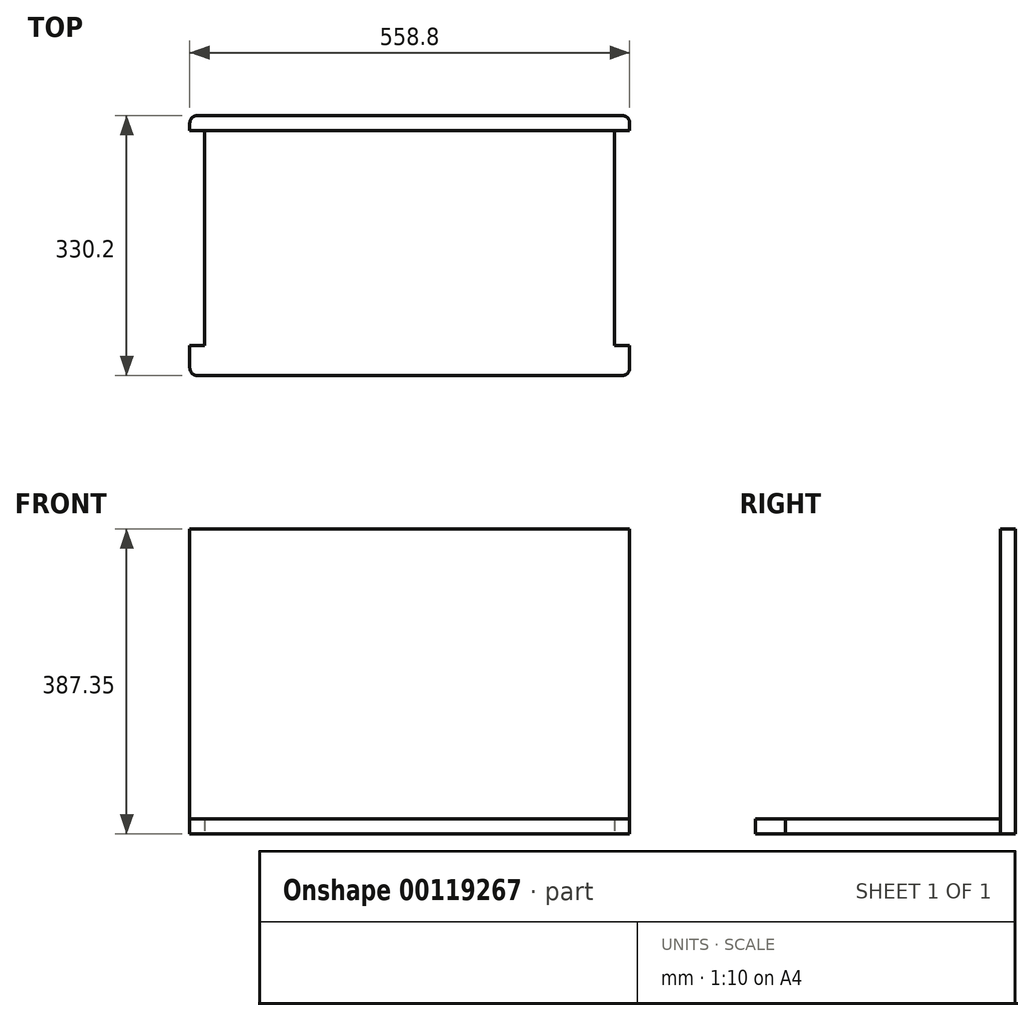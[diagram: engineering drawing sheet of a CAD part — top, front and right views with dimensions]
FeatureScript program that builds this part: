
annotation { "Feature Type Name" : "Feature", "Feature Type Description" : "" }
export const myFeature = defineFeature(function(context is Context, id is Id, definition is map)
    precondition{}
    {
        {
            var Q0;
            Q0=qCreatedBy(makeId("Top.planeOp"),FACE);
            var sketch = newSketch(context, id + "F0", { "sketchPlane" : qUnion([Q0])});
            skLineSegment(sketch, "E0.bottom", {"start": v(0, 0) * mm, "end": v(558.8, 0) * mm});
            skLineSegment(sketch, "E0.top", {"start": v(0, 330.2) * mm, "end": v(558.8, 330.2) * mm});
            skLineSegment(sketch, "E0.left", {"start": v(0, 0) * mm, "end": v(0, 330.2) * mm});
            skLineSegment(sketch, "E0.right", {"start": v(558.8, 0) * mm, "end": v(558.8, 330.2) * mm});
            skLineSegment(sketch, "E1.top", {"start": v(0, 311.15) * mm, "end": v(558.8, 311.15) * mm});
            skLineSegment(sketch, "E1.left", {"start": v(0, 330.2) * mm, "end": v(0, 311.15) * mm});
            skLineSegment(sketch, "E1.right", {"start": v(558.8, 330.2) * mm, "end": v(558.8, 311.15) * mm});
            skLineSegment(sketch, "E2.bottom", {"start": v(0, 311.15) * mm, "end": v(19.05, 311.15) * mm});
            skLineSegment(sketch, "E2.top", {"start": v(0, 38.1) * mm, "end": v(19.05, 38.1) * mm});
            skLineSegment(sketch, "E2.left", {"start": v(0, 311.15) * mm, "end": v(0, 38.1) * mm});
            skLineSegment(sketch, "E2.right", {"start": v(19.05, 311.15) * mm, "end": v(19.05, 38.1) * mm});
            skLineSegment(sketch, "E3.bottom", {"start": v(558.8, 311.15) * mm, "end": v(539.75, 311.15) * mm});
            skLineSegment(sketch, "E3.top", {"start": v(558.8, 38.1) * mm, "end": v(539.75, 38.1) * mm});
            skLineSegment(sketch, "E3.left", {"start": v(558.8, 311.15) * mm, "end": v(558.8, 38.1) * mm});
            skLineSegment(sketch, "E3.right", {"start": v(539.75, 311.15) * mm, "end": v(539.75, 38.1) * mm});
            skSolve(sketch);
        }
        {
            var Q0;
            Q0=makeQuery(id+"F0.imprint","IMPRINT",FACE,{"disambiguationData":[TD([[makeQuery(id+"F0.imprint","IMPRINT",EDGE,{"derivedFrom":sQuery(id+"F0.wireOp",EDGE,"E0.bottom")}),1.0]])]});
            extrude(context, id + "F1", {"entities" : qUnion([Q0]), "depth" : 19.05 * mm});
        }
        {
            var Q0;
            Q0=makeQuery(id+"F0.imprint","IMPRINT",FACE,{"disambiguationData":[TD([[makeQuery(id+"F0.imprint","IMPRINT",EDGE,{"derivedFrom":sQuery(id+"F0.wireOp",EDGE,"E0.top")}),-1.0]])]});
            var Q1;
            Q1=makeQuery(id+"F0.imprint","IMPRINT",FACE,{"disambiguationData":[TD([[makeQuery(id+"F0.imprint","IMPRINT",EDGE,{"derivedFrom":sQuery(id+"F0.wireOp",EDGE,"E2.bottom")}),-1.0]])]});
            var Q2;
            Q2=makeQuery(id+"F0.imprint","IMPRINT",FACE,{"disambiguationData":[TD([[makeQuery(id+"F0.imprint","IMPRINT",EDGE,{"derivedFrom":sQuery(id+"F0.wireOp",EDGE,"E3.bottom")}),1.0]])]});
            extrude(context, id + "F2", {"entities" : qUnion([Q0, Q1, Q2]), "operationType" : NewBodyOperationType.ADD, "depth" : 387.35 * mm});
        }
        {
            var Q0;
            Q0=makeQuery(id+"F2.opExtrude","SWEPT_EDGE",EDGE,{"disambiguationData":[OSD([sQuery(id+"F0.wireOp",EDGE,"E0.top"),sQuery(id+"F0.wireOp",EDGE,"E1.left")])]});
            var Q1;
            Q1=makeQuery(id+"F2.opExtrude","SWEPT_EDGE",EDGE,{"disambiguationData":[OSD([sQuery(id+"F0.wireOp",EDGE,"E0.top"),sQuery(id+"F0.wireOp",EDGE,"E1.right")])]});
            var Q2;
            Q2=makeQuery(id+"F1.opExtrude","SWEPT_EDGE",EDGE,{"disambiguationData":[OSD([sQuery(id+"F0.wireOp",EDGE,"E0.bottom"),sQuery(id+"F0.wireOp",EDGE,"E0.right")])]});
            var Q3;
            Q3=makeQuery(id+"F1.opExtrude","SWEPT_EDGE",EDGE,{"disambiguationData":[OSD([sQuery(id+"F0.wireOp",EDGE,"E0.bottom"),sQuery(id+"F0.wireOp",EDGE,"E0.left")])]});
            fillet(context, id + "F3", {"entities" : qUnion([Q0, Q1, Q2, Q3]), "radius" : 9.52 * mm, "tangentPropagation" : true, "allowEdgeOverflow" : false});
        }
    });
